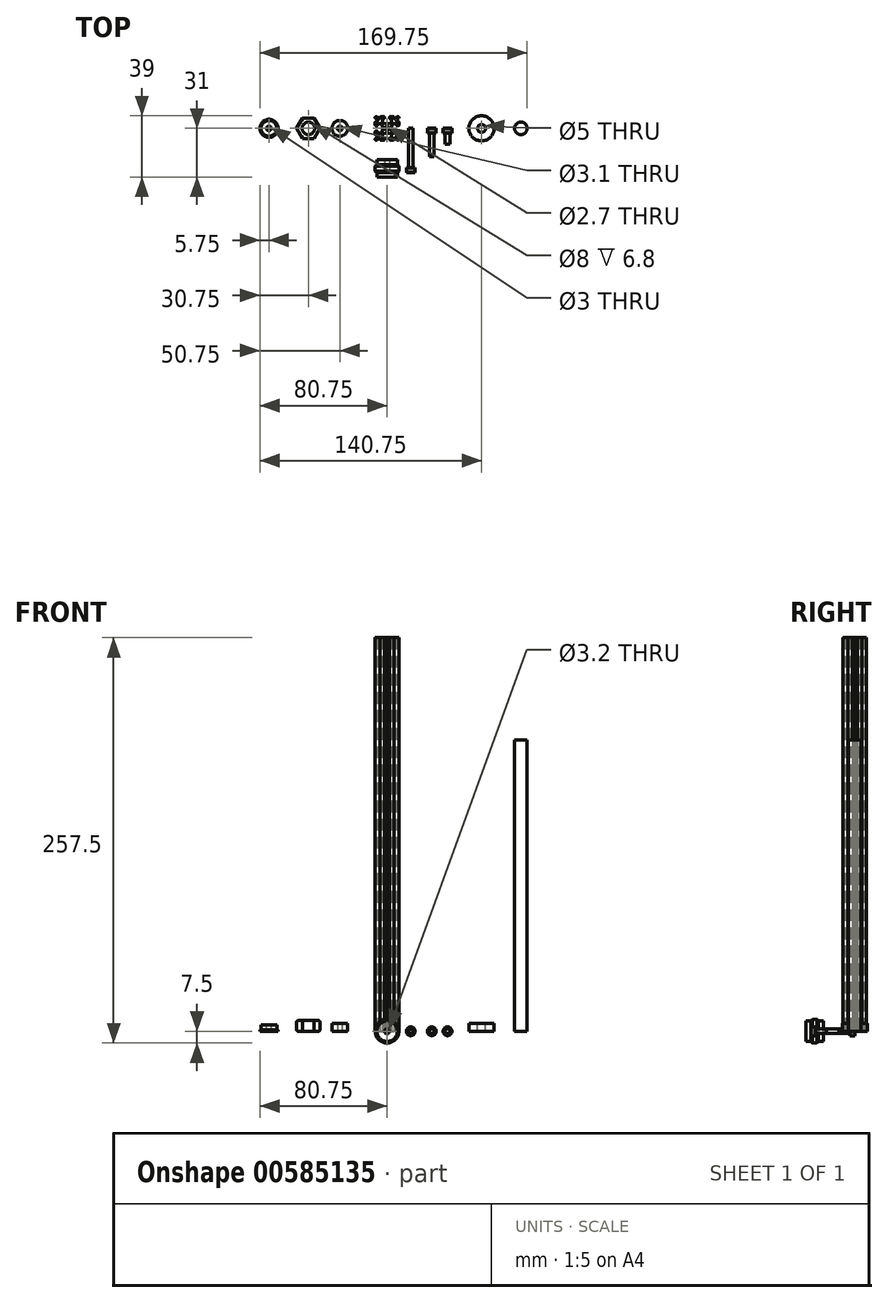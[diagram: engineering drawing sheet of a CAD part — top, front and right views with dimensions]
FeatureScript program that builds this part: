
annotation { "Feature Type Name" : "Feature", "Feature Type Description" : "" }
export const myFeature = defineFeature(function(context is Context, id is Id, definition is map)
    precondition{}
    {
        {
            var Q0;
            Q0=qCreatedBy(makeId("Top.planeOp"),FACE);
            var sketch = newSketch(context, id + "F0", { "sketchPlane" : qUnion([Q0])});
            skLineSegment(sketch, "E0", {"start": v(0, 0) * mm, "end": v(-7.5, -7.5) * mm, "construction": true});
            skArc(sketch, "E1", {"start": v(-1.35, 0) * mm, "mid": v(-1.25, -0.52) * mm, "end": v(-0.95, -0.95) * mm});
            skLineSegment(sketch, "E2", {"start": v(-7.5, -7) * mm, "end": v(-7.5, -6.72) * mm});
            skLineSegment(sketch, "E3", {"start": v(-7.35, -6.36) * mm, "end": v(-6.25, -5.26) * mm});
            skLineSegment(sketch, "E4", {"start": v(-6.6, -4.4) * mm, "end": v(-7, -4.4) * mm});
            skLineSegment(sketch, "E5", {"start": v(-7.5, -3.9) * mm, "end": v(-7.5, -2.1) * mm});
            skLineSegment(sketch, "E6", {"start": v(-7, -1.6) * mm, "end": v(-6.6, -1.6) * mm});
            skLineSegment(sketch, "E7", {"start": v(-6.1, -2.1) * mm, "end": v(-6.1, -2.7) * mm});
            skLineSegment(sketch, "E8", {"start": v(-5.9, -2.9) * mm, "end": v(-3.74, -2.9) * mm});
            skLineSegment(sketch, "E9", {"start": v(-3.25, -2.49) * mm, "end": v(-2.93, -0.73) * mm});
            skLineSegment(sketch, "E10", {"start": v(-2.73, -0.57) * mm, "end": v(-2.6, -0.57) * mm});
            skLineSegment(sketch, "E11", {"start": v(-2.4, -0.37) * mm, "end": v(-2.4, 0) * mm});
            skLineSegment(sketch, "E12", {"start": v(-2.4, 0) * mm, "end": v(-1.35, 0) * mm, "construction": true});
            skPoint(sketch, "E13.visualSharp", {"position": v(-5.4, -4.4) * mm});
            skArc(sketch, "E13.filletArc", {"start": v(-6.25, -5.26) * mm, "mid": v(-6.14, -4.71) * mm, "end": v(-6.6, -4.4) * mm});
            skPoint(sketch, "E14.visualSharp", {"position": v(-6.1, -2.9) * mm});
            skArc(sketch, "E14.filletArc", {"start": v(-6.1, -2.7) * mm, "mid": v(-6.04, -2.84) * mm, "end": v(-5.9, -2.9) * mm});
            skPoint(sketch, "E15.visualSharp", {"position": v(-6.1, -1.6) * mm});
            skArc(sketch, "E15.filletArc", {"start": v(-6.1, -2.1) * mm, "mid": v(-6.25, -1.75) * mm, "end": v(-6.6, -1.6) * mm});
            skPoint(sketch, "E16.visualSharp", {"position": v(-7.5, -1.6) * mm});
            skArc(sketch, "E16.filletArc", {"start": v(-7, -1.6) * mm, "mid": v(-7.35, -1.75) * mm, "end": v(-7.5, -2.1) * mm});
            skPoint(sketch, "E17.visualSharp", {"position": v(-7.5, -4.4) * mm});
            skArc(sketch, "E17.filletArc", {"start": v(-7.5, -3.9) * mm, "mid": v(-7.35, -4.26) * mm, "end": v(-7, -4.4) * mm});
            skPoint(sketch, "E18.visualSharp", {"position": v(-7.5, -6.51) * mm});
            skArc(sketch, "E18.filletArc", {"start": v(-7.35, -6.36) * mm, "mid": v(-7.46, -6.53) * mm, "end": v(-7.5, -6.72) * mm});
            skPoint(sketch, "E19.visualSharp", {"position": v(-3.32, -2.9) * mm});
            skArc(sketch, "E19.filletArc", {"start": v(-3.74, -2.9) * mm, "mid": v(-3.42, -2.78) * mm, "end": v(-3.25, -2.49) * mm});
            skPoint(sketch, "E20.visualSharp", {"position": v(-2.9, -0.57) * mm});
            skArc(sketch, "E20.filletArc", {"start": v(-2.73, -0.57) * mm, "mid": v(-2.86, -0.62) * mm, "end": v(-2.93, -0.73) * mm});
            skPoint(sketch, "E21.visualSharp", {"position": v(-2.4, -0.57) * mm});
            skArc(sketch, "E21.filletArc", {"start": v(-2.6, -0.57) * mm, "mid": v(-2.46, -0.51) * mm, "end": v(-2.4, -0.37) * mm});
            skLineSegment(sketch, "E22.0.MirrorCS", {"start": v(0, -2.4) * mm, "end": v(0, -1.35) * mm, "construction": true});
            skPoint(sketch, "E22.1.MirrorP", {"position": v(-4.4, -7.5) * mm});
            skArc(sketch, "E22.2.MirrorCS", {"start": v(-6.36, -7.35) * mm, "mid": v(-6.53, -7.46) * mm, "end": v(-6.72, -7.5) * mm});
            skPoint(sketch, "E22.3.MirrorP", {"position": v(-1.6, -7.5) * mm});
            skArc(sketch, "E22.4.MirrorCS", {"start": v(-1.6, -7) * mm, "mid": v(-1.75, -7.35) * mm, "end": v(-2.1, -7.5) * mm});
            skArc(sketch, "E22.5.MirrorCS", {"start": v(-0.57, -2.73) * mm, "mid": v(-0.62, -2.86) * mm, "end": v(-0.73, -2.93) * mm});
            skPoint(sketch, "E22.6.MirrorP", {"position": v(-1.6, -6.1) * mm});
            skLineSegment(sketch, "E22.7.MirrorCS", {"start": v(-3.9, -7.5) * mm, "end": v(-2.1, -7.5) * mm});
            skArc(sketch, "E22.8.MirrorCS", {"start": v(-5.26, -6.25) * mm, "mid": v(-4.71, -6.14) * mm, "end": v(-4.4, -6.6) * mm});
            skPoint(sketch, "E22.9.MirrorP", {"position": v(-0.57, -2.4) * mm});
            skPoint(sketch, "E22.10.MirrorP", {"position": v(-4.4, -5.4) * mm});
            skArc(sketch, "E22.11.MirrorCS", {"start": v(-2.7, -6.1) * mm, "mid": v(-2.84, -6.04) * mm, "end": v(-2.9, -5.9) * mm});
            skPoint(sketch, "E22.12.MirrorP", {"position": v(-0.57, -2.9) * mm});
            skLineSegment(sketch, "E22.13.MirrorCS", {"start": v(-7, -7.5) * mm, "end": v(-6.72, -7.5) * mm});
            skLineSegment(sketch, "E22.14.MirrorCS", {"start": v(-1.6, -7) * mm, "end": v(-1.6, -6.6) * mm});
            skLineSegment(sketch, "E22.15.MirrorCS", {"start": v(-6.36, -7.35) * mm, "end": v(-5.26, -6.25) * mm});
            skArc(sketch, "E22.16.MirrorCS", {"start": v(-2.1, -6.1) * mm, "mid": v(-1.75, -6.25) * mm, "end": v(-1.6, -6.6) * mm});
            skLineSegment(sketch, "E22.17.MirrorCS", {"start": v(-4.4, -6.6) * mm, "end": v(-4.4, -7) * mm});
            skArc(sketch, "E22.18.MirrorCS", {"start": v(-2.9, -3.74) * mm, "mid": v(-2.78, -3.42) * mm, "end": v(-2.49, -3.25) * mm});
            skLineSegment(sketch, "E22.19.MirrorCS", {"start": v(-2.9, -5.9) * mm, "end": v(-2.9, -3.74) * mm});
            skLineSegment(sketch, "E22.20.MirrorCS", {"start": v(-2.1, -6.1) * mm, "end": v(-2.7, -6.1) * mm});
            skArc(sketch, "E22.21.MirrorCS", {"start": v(-0.57, -2.6) * mm, "mid": v(-0.51, -2.46) * mm, "end": v(-0.37, -2.4) * mm});
            skLineSegment(sketch, "E22.22.MirrorCS", {"start": v(-0.37, -2.4) * mm, "end": v(0, -2.4) * mm});
            skPoint(sketch, "E22.23.MirrorP", {"position": v(-6.51, -7.5) * mm});
            skPoint(sketch, "E22.24.MirrorP", {"position": v(-2.9, -6.1) * mm});
            skLineSegment(sketch, "E22.25.MirrorCS", {"start": v(-2.49, -3.25) * mm, "end": v(-0.73, -2.93) * mm});
            skLineSegment(sketch, "E22.26.MirrorCS", {"start": v(-0.57, -2.73) * mm, "end": v(-0.57, -2.6) * mm});
            skArc(sketch, "E22.27.MirrorCS", {"start": v(0, -1.35) * mm, "mid": v(-0.52, -1.25) * mm, "end": v(-0.95, -0.95) * mm});
            skArc(sketch, "E22.28.MirrorCS", {"start": v(-3.9, -7.5) * mm, "mid": v(-4.26, -7.35) * mm, "end": v(-4.4, -7) * mm});
            skPoint(sketch, "E22.29.MirrorP", {"position": v(-2.9, -3.32) * mm});
            skPoint(sketch, "E23.visualSharp", {"position": v(-7.5, -7.5) * mm});
            skArc(sketch, "E23.filletArc", {"start": v(-7.5, -7) * mm, "mid": v(-7.35, -7.35) * mm, "end": v(-7, -7.5) * mm});
            skLineSegment(sketch, "E24.0.MirrorCS", {"start": v(0, 2.4) * mm, "end": v(0, 1.35) * mm, "construction": true});
            skLineSegment(sketch, "E24.1.MirrorCS", {"start": v(-2.1, 6.1) * mm, "end": v(-2.7, 6.1) * mm});
            skLineSegment(sketch, "E24.2.MirrorCS", {"start": v(-7.5, 3.9) * mm, "end": v(-7.5, 2.1) * mm});
            skLineSegment(sketch, "E24.3.MirrorCS", {"start": v(-7, 1.6) * mm, "end": v(-6.6, 1.6) * mm});
            skArc(sketch, "E24.4.MirrorCS", {"start": v(-6.1, 2.1) * mm, "mid": v(-6.25, 1.75) * mm, "end": v(-6.6, 1.6) * mm});
            skPoint(sketch, "E24.5.MirrorP", {"position": v(-3.32, 2.9) * mm});
            skPoint(sketch, "E24.6.MirrorP", {"position": v(-0.57, 2.9) * mm});
            skArc(sketch, "E24.7.MirrorCS", {"start": v(-0.57, 2.6) * mm, "mid": v(-0.51, 2.46) * mm, "end": v(-0.37, 2.4) * mm});
            skArc(sketch, "E24.8.MirrorCS", {"start": v(-2.6, 0.57) * mm, "mid": v(-2.46, 0.51) * mm, "end": v(-2.4, 0.37) * mm});
            skLineSegment(sketch, "E24.9.MirrorCS", {"start": v(-0.37, 2.4) * mm, "end": v(0, 2.4) * mm});
            skArc(sketch, "E24.10.MirrorCS", {"start": v(-6.1, 2.7) * mm, "mid": v(-6.04, 2.84) * mm, "end": v(-5.9, 2.9) * mm});
            skPoint(sketch, "E24.11.MirrorP", {"position": v(-4.4, 5.4) * mm});
            skLineSegment(sketch, "E24.12.MirrorCS", {"start": v(-2.9, 5.9) * mm, "end": v(-2.9, 3.74) * mm});
            skLineSegment(sketch, "E24.13.MirrorCS", {"start": v(-7.35, 6.36) * mm, "end": v(-6.25, 5.26) * mm});
            skPoint(sketch, "E24.14.MirrorP", {"position": v(-7.5, 6.51) * mm});
            skArc(sketch, "E24.15.MirrorCS", {"start": v(-3.74, 2.9) * mm, "mid": v(-3.42, 2.78) * mm, "end": v(-3.25, 2.49) * mm});
            skArc(sketch, "E24.16.MirrorCS", {"start": v(-2.1, 6.1) * mm, "mid": v(-1.75, 6.25) * mm, "end": v(-1.6, 6.6) * mm});
            skArc(sketch, "E24.17.MirrorCS", {"start": v(-7, 1.6) * mm, "mid": v(-7.35, 1.75) * mm, "end": v(-7.5, 2.1) * mm});
            skPoint(sketch, "E24.18.MirrorP", {"position": v(-1.6, 6.1) * mm});
            skPoint(sketch, "E24.19.MirrorP", {"position": v(-7.5, 4.4) * mm});
            skLineSegment(sketch, "E24.20.MirrorCS", {"start": v(-4.4, 6.6) * mm, "end": v(-4.4, 7) * mm});
            skArc(sketch, "E24.21.MirrorCS", {"start": v(-7.5, 3.9) * mm, "mid": v(-7.35, 4.26) * mm, "end": v(-7, 4.4) * mm});
            skPoint(sketch, "E24.22.MirrorP", {"position": v(-0.57, 2.4) * mm});
            skLineSegment(sketch, "E24.23.MirrorCS", {"start": v(-5.9, 2.9) * mm, "end": v(-3.74, 2.9) * mm});
            skArc(sketch, "E24.24.MirrorCS", {"start": v(-2.9, 3.74) * mm, "mid": v(-2.78, 3.42) * mm, "end": v(-2.49, 3.25) * mm});
            skArc(sketch, "E24.25.MirrorCS", {"start": v(-7.35, 6.36) * mm, "mid": v(-7.46, 6.53) * mm, "end": v(-7.5, 6.72) * mm});
            skPoint(sketch, "E24.26.MirrorP", {"position": v(-6.1, 2.9) * mm});
            skPoint(sketch, "E24.27.MirrorP", {"position": v(-4.4, 7.5) * mm});
            skArc(sketch, "E24.28.MirrorCS", {"start": v(-5.26, 6.25) * mm, "mid": v(-4.71, 6.14) * mm, "end": v(-4.4, 6.6) * mm});
            skArc(sketch, "E24.29.MirrorCS", {"start": v(-7.5, 7) * mm, "mid": v(-7.35, 7.35) * mm, "end": v(-7, 7.5) * mm});
            skPoint(sketch, "E24.30.MirrorP", {"position": v(-6.1, 1.6) * mm});
            skPoint(sketch, "E24.31.MirrorP", {"position": v(-2.9, 3.32) * mm});
            skPoint(sketch, "E24.32.MirrorP", {"position": v(-1.6, 7.5) * mm});
            skPoint(sketch, "E24.33.MirrorP", {"position": v(-2.9, 6.1) * mm});
            skLineSegment(sketch, "E24.34.MirrorCS", {"start": v(-3.9, 7.5) * mm, "end": v(-2.1, 7.5) * mm});
            skLineSegment(sketch, "E24.35.MirrorCS", {"start": v(-7, 7.5) * mm, "end": v(-6.72, 7.5) * mm});
            skArc(sketch, "E24.36.MirrorCS", {"start": v(-3.9, 7.5) * mm, "mid": v(-4.26, 7.35) * mm, "end": v(-4.4, 7) * mm});
            skPoint(sketch, "E24.37.MirrorP", {"position": v(-7.5, 7.5) * mm});
            skLineSegment(sketch, "E24.38.MirrorCS", {"start": v(-1.6, 7) * mm, "end": v(-1.6, 6.6) * mm});
            skLineSegment(sketch, "E24.39.MirrorCS", {"start": v(-6.36, 7.35) * mm, "end": v(-5.26, 6.25) * mm});
            skPoint(sketch, "E24.40.MirrorP", {"position": v(-7.5, 1.6) * mm});
            skArc(sketch, "E24.41.MirrorCS", {"start": v(-2.7, 6.1) * mm, "mid": v(-2.84, 6.04) * mm, "end": v(-2.9, 5.9) * mm});
            skArc(sketch, "E24.42.MirrorCS", {"start": v(-6.36, 7.35) * mm, "mid": v(-6.53, 7.46) * mm, "end": v(-6.72, 7.5) * mm});
            skLineSegment(sketch, "E24.43.MirrorCS", {"start": v(-2.49, 3.25) * mm, "end": v(-0.73, 2.93) * mm});
            skPoint(sketch, "E24.44.MirrorP", {"position": v(-2.9, 0.57) * mm});
            skLineSegment(sketch, "E24.45.MirrorCS", {"start": v(-6.6, 4.4) * mm, "end": v(-7, 4.4) * mm});
            skArc(sketch, "E24.46.MirrorCS", {"start": v(-1.6, 7) * mm, "mid": v(-1.75, 7.35) * mm, "end": v(-2.1, 7.5) * mm});
            skArc(sketch, "E24.47.MirrorCS", {"start": v(-2.73, 0.57) * mm, "mid": v(-2.86, 0.62) * mm, "end": v(-2.93, 0.73) * mm});
            skArc(sketch, "E24.48.MirrorCS", {"start": v(-6.25, 5.26) * mm, "mid": v(-6.14, 4.71) * mm, "end": v(-6.6, 4.4) * mm});
            skLineSegment(sketch, "E24.49.MirrorCS", {"start": v(-0.57, 2.73) * mm, "end": v(-0.57, 2.6) * mm});
            skLineSegment(sketch, "E24.50.MirrorCS", {"start": v(-2.73, 0.57) * mm, "end": v(-2.6, 0.57) * mm});
            skArc(sketch, "E24.51.MirrorCS", {"start": v(-1.35, 0) * mm, "mid": v(-1.25, 0.52) * mm, "end": v(-0.95, 0.95) * mm});
            skPoint(sketch, "E24.52.MirrorP", {"position": v(-2.4, 0.57) * mm});
            skPoint(sketch, "E24.53.MirrorP", {"position": v(-5.4, 4.4) * mm});
            skLineSegment(sketch, "E24.54.MirrorCS", {"start": v(-2.4, 0.37) * mm, "end": v(-2.4, 0) * mm});
            skArc(sketch, "E24.55.MirrorCS", {"start": v(0, 1.35) * mm, "mid": v(-0.52, 1.25) * mm, "end": v(-0.95, 0.95) * mm});
            skLineSegment(sketch, "E24.56.MirrorCS", {"start": v(-3.25, 2.49) * mm, "end": v(-2.93, 0.73) * mm});
            skLineSegment(sketch, "E24.57.MirrorCS", {"start": v(-6.1, 2.1) * mm, "end": v(-6.1, 2.7) * mm});
            skLineSegment(sketch, "E24.58.MirrorCS", {"start": v(-7.5, 7) * mm, "end": v(-7.5, 6.72) * mm});
            skArc(sketch, "E24.59.MirrorCS", {"start": v(-0.57, 2.73) * mm, "mid": v(-0.62, 2.86) * mm, "end": v(-0.73, 2.93) * mm});
            skPoint(sketch, "E24.60.MirrorP", {"position": v(-6.51, 7.5) * mm});
            skLineSegment(sketch, "E25.0.MirrorCS", {"start": v(7, -7.5) * mm, "end": v(6.72, -7.5) * mm});
            skLineSegment(sketch, "E25.1.MirrorCS", {"start": v(0.57, 2.73) * mm, "end": v(0.57, 2.6) * mm});
            skLineSegment(sketch, "E25.2.MirrorCS", {"start": v(0.37, 2.4) * mm, "end": v(0, 2.4) * mm});
            skLineSegment(sketch, "E25.3.MirrorCS", {"start": v(7, 7.5) * mm, "end": v(6.72, 7.5) * mm});
            skLineSegment(sketch, "E25.4.MirrorCS", {"start": v(1.6, -7) * mm, "end": v(1.6, -6.6) * mm});
            skLineSegment(sketch, "E25.5.MirrorCS", {"start": v(2.73, 0.57) * mm, "end": v(2.6, 0.57) * mm});
            skLineSegment(sketch, "E25.6.MirrorCS", {"start": v(7, 1.6) * mm, "end": v(6.6, 1.6) * mm});
            skLineSegment(sketch, "E25.7.MirrorCS", {"start": v(5.9, 2.9) * mm, "end": v(3.74, 2.9) * mm});
            skLineSegment(sketch, "E25.8.MirrorCS", {"start": v(7.35, 6.36) * mm, "end": v(6.25, 5.26) * mm});
            skArc(sketch, "E25.9.MirrorCS", {"start": v(2.7, -6.1) * mm, "mid": v(2.84, -6.04) * mm, "end": v(2.9, -5.9) * mm});
            skArc(sketch, "E25.10.MirrorCS", {"start": v(2.9, 3.74) * mm, "mid": v(2.78, 3.42) * mm, "end": v(2.49, 3.25) * mm});
            skPoint(sketch, "E25.11.MirrorP", {"position": v(1.6, -7.5) * mm});
            skPoint(sketch, "E25.12.MirrorP", {"position": v(6.1, -1.6) * mm});
            skPoint(sketch, "E25.13.MirrorP", {"position": v(2.9, 3.32) * mm});
            skPoint(sketch, "E25.14.MirrorP", {"position": v(7.5, -1.6) * mm});
            skArc(sketch, "E25.15.MirrorCS", {"start": v(1.6, 7) * mm, "mid": v(1.75, 7.35) * mm, "end": v(2.1, 7.5) * mm});
            skLineSegment(sketch, "E25.16.MirrorCS", {"start": v(6.1, -2.1) * mm, "end": v(6.1, -2.7) * mm});
            skLineSegment(sketch, "E25.17.MirrorCS", {"start": v(2.4, 0.37) * mm, "end": v(2.4, 0) * mm});
            skArc(sketch, "E25.18.MirrorCS", {"start": v(7, -1.6) * mm, "mid": v(7.35, -1.75) * mm, "end": v(7.5, -2.1) * mm});
            skArc(sketch, "E25.19.MirrorCS", {"start": v(7.5, 7) * mm, "mid": v(7.35, 7.35) * mm, "end": v(7, 7.5) * mm});
            skArc(sketch, "E25.20.MirrorCS", {"start": v(2.1, -6.1) * mm, "mid": v(1.75, -6.25) * mm, "end": v(1.6, -6.6) * mm});
            skArc(sketch, "E25.21.MirrorCS", {"start": v(6.1, 2.1) * mm, "mid": v(6.25, 1.75) * mm, "end": v(6.6, 1.6) * mm});
            skLineSegment(sketch, "E25.22.MirrorCS", {"start": v(4.4, 6.6) * mm, "end": v(4.4, 7) * mm});
            skLineSegment(sketch, "E25.23.MirrorCS", {"start": v(6.6, 4.4) * mm, "end": v(7, 4.4) * mm});
            skArc(sketch, "E25.24.MirrorCS", {"start": v(7, 1.6) * mm, "mid": v(7.35, 1.75) * mm, "end": v(7.5, 2.1) * mm});
            skArc(sketch, "E25.25.MirrorCS", {"start": v(0, -1.35) * mm, "mid": v(0.52, -1.25) * mm, "end": v(0.95, -0.95) * mm});
            skLineSegment(sketch, "E25.26.MirrorCS", {"start": v(3.9, -7.5) * mm, "end": v(2.1, -7.5) * mm});
            skLineSegment(sketch, "E25.27.MirrorCS", {"start": v(2.1, 6.1) * mm, "end": v(2.7, 6.1) * mm});
            skLineSegment(sketch, "E25.28.MirrorCS", {"start": v(2.73, -0.57) * mm, "end": v(2.6, -0.57) * mm});
            skLineSegment(sketch, "E25.29.MirrorCS", {"start": v(4.4, -6.6) * mm, "end": v(4.4, -7) * mm});
            skLineSegment(sketch, "E25.30.MirrorCS", {"start": v(3.9, 7.5) * mm, "end": v(2.1, 7.5) * mm});
            skArc(sketch, "E25.31.MirrorCS", {"start": v(0.57, -2.73) * mm, "mid": v(0.62, -2.86) * mm, "end": v(0.73, -2.93) * mm});
            skArc(sketch, "E25.32.MirrorCS", {"start": v(0.57, 2.6) * mm, "mid": v(0.51, 2.46) * mm, "end": v(0.37, 2.4) * mm});
            skPoint(sketch, "E25.33.MirrorP", {"position": v(6.51, -7.5) * mm});
            skArc(sketch, "E25.34.MirrorCS", {"start": v(3.9, -7.5) * mm, "mid": v(4.26, -7.35) * mm, "end": v(4.4, -7) * mm});
            skArc(sketch, "E25.35.MirrorCS", {"start": v(2.7, 6.1) * mm, "mid": v(2.84, 6.04) * mm, "end": v(2.9, 5.9) * mm});
            skPoint(sketch, "E25.36.MirrorP", {"position": v(0.57, -2.4) * mm});
            skPoint(sketch, "E25.37.MirrorP", {"position": v(0.57, 2.9) * mm});
            skLineSegment(sketch, "E25.38.MirrorCS", {"start": v(3.25, -2.49) * mm, "end": v(2.93, -0.73) * mm});
            skPoint(sketch, "E25.39.MirrorP", {"position": v(5.4, -4.4) * mm});
            skPoint(sketch, "E25.40.MirrorP", {"position": v(2.4, -0.57) * mm});
            skLineSegment(sketch, "E25.41.MirrorCS", {"start": v(7.5, -7) * mm, "end": v(7.5, -6.72) * mm});
            skArc(sketch, "E25.42.MirrorCS", {"start": v(7.35, 6.36) * mm, "mid": v(7.46, 6.53) * mm, "end": v(7.5, 6.72) * mm});
            skPoint(sketch, "E25.43.MirrorP", {"position": v(4.4, 7.5) * mm});
            skArc(sketch, "E25.44.MirrorCS", {"start": v(6.25, 5.26) * mm, "mid": v(6.14, 4.71) * mm, "end": v(6.6, 4.4) * mm});
            skPoint(sketch, "E25.45.MirrorP", {"position": v(6.1, -2.9) * mm});
            skPoint(sketch, "E25.46.MirrorP", {"position": v(4.4, -7.5) * mm});
            skArc(sketch, "E25.47.MirrorCS", {"start": v(6.1, 2.7) * mm, "mid": v(6.04, 2.84) * mm, "end": v(5.9, 2.9) * mm});
            skLineSegment(sketch, "E25.48.MirrorCS", {"start": v(2.1, -6.1) * mm, "end": v(2.7, -6.1) * mm});
            skArc(sketch, "E25.49.MirrorCS", {"start": v(2.73, -0.57) * mm, "mid": v(2.86, -0.62) * mm, "end": v(2.93, -0.73) * mm});
            skArc(sketch, "E25.50.MirrorCS", {"start": v(7.35, -6.36) * mm, "mid": v(7.46, -6.53) * mm, "end": v(7.5, -6.72) * mm});
            skLineSegment(sketch, "E25.51.MirrorCS", {"start": v(3.25, 2.49) * mm, "end": v(2.93, 0.73) * mm});
            skArc(sketch, "E25.52.MirrorCS", {"start": v(2.9, -3.74) * mm, "mid": v(2.78, -3.42) * mm, "end": v(2.49, -3.25) * mm});
            skArc(sketch, "E25.53.MirrorCS", {"start": v(2.6, 0.57) * mm, "mid": v(2.46, 0.51) * mm, "end": v(2.4, 0.37) * mm});
            skPoint(sketch, "E25.54.MirrorP", {"position": v(2.9, 0.57) * mm});
            skPoint(sketch, "E25.55.MirrorP", {"position": v(7.5, -6.51) * mm});
            skLineSegment(sketch, "E25.56.MirrorCS", {"start": v(2.49, 3.25) * mm, "end": v(0.73, 2.93) * mm});
            skArc(sketch, "E25.57.MirrorCS", {"start": v(1.6, -7) * mm, "mid": v(1.75, -7.35) * mm, "end": v(2.1, -7.5) * mm});
            skArc(sketch, "E25.58.MirrorCS", {"start": v(2.1, 6.1) * mm, "mid": v(1.75, 6.25) * mm, "end": v(1.6, 6.6) * mm});
            skLineSegment(sketch, "E25.59.MirrorCS", {"start": v(0.57, -2.73) * mm, "end": v(0.57, -2.6) * mm});
            skLineSegment(sketch, "E25.60.MirrorCS", {"start": v(2.4, -0.37) * mm, "end": v(2.4, 0) * mm});
            skArc(sketch, "E25.61.MirrorCS", {"start": v(7.5, -3.9) * mm, "mid": v(7.35, -4.26) * mm, "end": v(7, -4.4) * mm});
            skLineSegment(sketch, "E25.62.MirrorCS", {"start": v(5.9, -2.9) * mm, "end": v(3.74, -2.9) * mm});
            skLineSegment(sketch, "E25.63.MirrorCS", {"start": v(7.5, -3.9) * mm, "end": v(7.5, -2.1) * mm});
            skLineSegment(sketch, "E25.64.MirrorCS", {"start": v(7, -1.6) * mm, "end": v(6.6, -1.6) * mm});
            skArc(sketch, "E25.65.MirrorCS", {"start": v(1.35, 0) * mm, "mid": v(1.25, -0.52) * mm, "end": v(0.95, -0.95) * mm});
            skPoint(sketch, "E25.66.MirrorP", {"position": v(7.5, 1.6) * mm});
            skPoint(sketch, "E25.67.MirrorP", {"position": v(1.6, 6.1) * mm});
            skLineSegment(sketch, "E25.68.MirrorCS", {"start": v(6.36, -7.35) * mm, "end": v(5.26, -6.25) * mm});
            skPoint(sketch, "E25.69.MirrorP", {"position": v(2.4, 0.57) * mm});
            skPoint(sketch, "E25.70.MirrorP", {"position": v(6.1, 1.6) * mm});
            skPoint(sketch, "E25.71.MirrorP", {"position": v(3.32, -2.9) * mm});
            skPoint(sketch, "E25.72.MirrorP", {"position": v(0.57, -2.9) * mm});
            skPoint(sketch, "E25.73.MirrorP", {"position": v(7.5, 4.4) * mm});
            skArc(sketch, "E25.74.MirrorCS", {"start": v(5.26, -6.25) * mm, "mid": v(4.71, -6.14) * mm, "end": v(4.4, -6.6) * mm});
            skArc(sketch, "E25.75.MirrorCS", {"start": v(7.5, -7) * mm, "mid": v(7.35, -7.35) * mm, "end": v(7, -7.5) * mm});
            skLineSegment(sketch, "E25.76.MirrorCS", {"start": v(2.49, -3.25) * mm, "end": v(0.73, -2.93) * mm});
            skArc(sketch, "E25.77.MirrorCS", {"start": v(3.74, 2.9) * mm, "mid": v(3.42, 2.78) * mm, "end": v(3.25, 2.49) * mm});
            skArc(sketch, "E25.78.MirrorCS", {"start": v(6.36, -7.35) * mm, "mid": v(6.53, -7.46) * mm, "end": v(6.72, -7.5) * mm});
            skArc(sketch, "E25.79.MirrorCS", {"start": v(7.5, 3.9) * mm, "mid": v(7.35, 4.26) * mm, "end": v(7, 4.4) * mm});
            skArc(sketch, "E25.80.MirrorCS", {"start": v(2.73, 0.57) * mm, "mid": v(2.86, 0.62) * mm, "end": v(2.93, 0.73) * mm});
            skArc(sketch, "E25.81.MirrorCS", {"start": v(6.36, 7.35) * mm, "mid": v(6.53, 7.46) * mm, "end": v(6.72, 7.5) * mm});
            skPoint(sketch, "E25.82.MirrorP", {"position": v(4.4, -5.4) * mm});
            skPoint(sketch, "E25.83.MirrorP", {"position": v(6.51, 7.5) * mm});
            skPoint(sketch, "E25.84.MirrorP", {"position": v(2.9, -0.57) * mm});
            skLineSegment(sketch, "E25.85.MirrorCS", {"start": v(2.9, -5.9) * mm, "end": v(2.9, -3.74) * mm});
            skLineSegment(sketch, "E25.86.MirrorCS", {"start": v(6.1, 2.1) * mm, "end": v(6.1, 2.7) * mm});
            skLineSegment(sketch, "E25.87.MirrorCS", {"start": v(6.36, 7.35) * mm, "end": v(5.26, 6.25) * mm});
            skArc(sketch, "E25.88.MirrorCS", {"start": v(0.57, 2.73) * mm, "mid": v(0.62, 2.86) * mm, "end": v(0.73, 2.93) * mm});
            skArc(sketch, "E25.89.MirrorCS", {"start": v(0.57, -2.6) * mm, "mid": v(0.51, -2.46) * mm, "end": v(0.37, -2.4) * mm});
            skLineSegment(sketch, "E25.90.MirrorCS", {"start": v(2.9, 5.9) * mm, "end": v(2.9, 3.74) * mm});
            skArc(sketch, "E25.91.MirrorCS", {"start": v(0, 1.35) * mm, "mid": v(0.52, 1.25) * mm, "end": v(0.95, 0.95) * mm});
            skArc(sketch, "E25.92.MirrorCS", {"start": v(2.6, -0.57) * mm, "mid": v(2.46, -0.51) * mm, "end": v(2.4, -0.37) * mm});
            skPoint(sketch, "E25.93.MirrorP", {"position": v(4.4, 5.4) * mm});
            skPoint(sketch, "E25.94.MirrorP", {"position": v(2.9, -3.32) * mm});
            skPoint(sketch, "E25.95.MirrorP", {"position": v(2.9, 6.1) * mm});
            skPoint(sketch, "E25.96.MirrorP", {"position": v(5.4, 4.4) * mm});
            skPoint(sketch, "E25.97.MirrorP", {"position": v(3.32, 2.9) * mm});
            skArc(sketch, "E25.98.MirrorCS", {"start": v(3.74, -2.9) * mm, "mid": v(3.42, -2.78) * mm, "end": v(3.25, -2.49) * mm});
            skArc(sketch, "E25.99.MirrorCS", {"start": v(3.9, 7.5) * mm, "mid": v(4.26, 7.35) * mm, "end": v(4.4, 7) * mm});
            skPoint(sketch, "E25.100.MirrorP", {"position": v(7.5, -4.4) * mm});
            skPoint(sketch, "E25.101.MirrorP", {"position": v(6.1, 2.9) * mm});
            skArc(sketch, "E25.102.MirrorCS", {"start": v(1.35, 0) * mm, "mid": v(1.25, 0.52) * mm, "end": v(0.95, 0.95) * mm});
            skArc(sketch, "E25.103.MirrorCS", {"start": v(5.26, 6.25) * mm, "mid": v(4.71, 6.14) * mm, "end": v(4.4, 6.6) * mm});
            skPoint(sketch, "E25.104.MirrorP", {"position": v(7.5, 6.51) * mm});
            skPoint(sketch, "E25.105.MirrorP", {"position": v(2.9, -6.1) * mm});
            skArc(sketch, "E25.106.MirrorCS", {"start": v(6.25, -5.26) * mm, "mid": v(6.14, -4.71) * mm, "end": v(6.6, -4.4) * mm});
            skArc(sketch, "E25.107.MirrorCS", {"start": v(6.1, -2.1) * mm, "mid": v(6.25, -1.75) * mm, "end": v(6.6, -1.6) * mm});
            skPoint(sketch, "E25.108.MirrorP", {"position": v(1.6, 7.5) * mm});
            skPoint(sketch, "E25.109.MirrorP", {"position": v(7.5, 7.5) * mm});
            skLineSegment(sketch, "E25.110.MirrorCS", {"start": v(0.37, -2.4) * mm, "end": v(0, -2.4) * mm});
            skPoint(sketch, "E25.111.MirrorP", {"position": v(7.5, -7.5) * mm});
            skLineSegment(sketch, "E25.112.MirrorCS", {"start": v(7.5, 7) * mm, "end": v(7.5, 6.72) * mm});
            skArc(sketch, "E25.113.MirrorCS", {"start": v(6.1, -2.7) * mm, "mid": v(6.04, -2.84) * mm, "end": v(5.9, -2.9) * mm});
            skLineSegment(sketch, "E25.114.MirrorCS", {"start": v(1.6, 7) * mm, "end": v(1.6, 6.6) * mm});
            skPoint(sketch, "E25.115.MirrorP", {"position": v(1.6, -6.1) * mm});
            skLineSegment(sketch, "E25.116.MirrorCS", {"start": v(7.35, -6.36) * mm, "end": v(6.25, -5.26) * mm});
            skLineSegment(sketch, "E25.117.MirrorCS", {"start": v(7.5, 3.9) * mm, "end": v(7.5, 2.1) * mm});
            skPoint(sketch, "E25.118.MirrorP", {"position": v(0.57, 2.4) * mm});
            skLineSegment(sketch, "E25.119.MirrorCS", {"start": v(6.6, -4.4) * mm, "end": v(7, -4.4) * mm});
            skSolve(sketch);
        }
        {
            var Q0;
            Q0=makeQuery(id+"F0.imprint","IMPRINT",FACE,{"disambiguationData":[TD([[makeQuery(id+"F0.imprint","IMPRINT",EDGE,{"derivedFrom":sQuery(id+"F0.wireOp",EDGE,"E1")}),-1.0]])]});
            extrude(context, id + "F1", {"entities" : qUnion([Q0]), "depth" : 250 * mm});
        }
        {
            var Q0;
            Q0=qCreatedBy(makeId("Right.planeOp"),FACE);
            var sketch = newSketch(context, id + "F2", { "sketchPlane" : qUnion([Q0])});
            skLineSegment(sketch, "E26", {"start": v(-31, 0) * mm, "end": v(-31, 6.5) * mm});
            skLineSegment(sketch, "E27", {"start": v(-20, 6.5) * mm, "end": v(-20, 0) * mm});
            skLineSegment(sketch, "E28", {"start": v(-20, 0) * mm, "end": v(-31, 0) * mm});
            skLineSegment(sketch, "E29", {"start": v(-31, 6.5) * mm, "end": v(-28, 6.5) * mm});
            skLineSegment(sketch, "E30", {"start": v(-28, 6.5) * mm, "end": v(-27, 7.5) * mm});
            skLineSegment(sketch, "E31", {"start": v(-27, 7.5) * mm, "end": v(-24, 7.5) * mm});
            skLineSegment(sketch, "E32", {"start": v(-24, 7.5) * mm, "end": v(-23, 6.5) * mm});
            skLineSegment(sketch, "E33", {"start": v(-23, 6.5) * mm, "end": v(-20, 6.5) * mm});
            skLineSegment(sketch, "E34", {"start": v(-25.5, 7.5) * mm, "end": v(-25.5, 0) * mm, "construction": true});
            skSolve(sketch);
        }
        {
            var Q0;
            Q0=qSketchRegion(id+"F2",true);
            var Q1;
            Q1=sQuery(id+"F2.wireOp",EDGE,"E28");
            revolve(context, id + "F3", {"entities" : qUnion([Q0]), "axis" : qUnion([Q1]), "revolveType" : RevolveType.FULL});
        }
        {
            var Q0;
            Q0=makeQuery(id+"F3.opRevolve","SWEPT_FACE",FACE,{"disambiguationData":[OSD([sQuery(id+"F2.wireOp",EDGE,"E26")])]});
            var sketch = newSketch(context, id + "F4", { "sketchPlane" : qUnion([Q0])});
            skCircle(sketch, "E35", {"center": v(0, 0) * mm, "radius": 1.6 * mm});
            skSolve(sketch);
        }
        {
            var Q0;
            Q0=makeQuery(id+"F4.imprint","IMPRINT",FACE,{"disambiguationData":[TD([[makeQuery(id+"F4.imprint","IMPRINT",EDGE,{"derivedFrom":sQuery(id+"F4.wireOp",EDGE,"E35")}),1.0]])]});
            extrude(context, id + "F5", {"entities" : qUnion([Q0]), "operationType" : NewBodyOperationType.REMOVE, "oppositeDirection" : true, "depth" : 11 * mm});
        }
        {
            var Q0;
            Q0=qCreatedBy(makeId("Front.planeOp"),FACE);
            var sketch = newSketch(context, id + "F6", { "sketchPlane" : qUnion([Q0])});
            skCircle(sketch, "E36", {"center": v(15, 0) * mm, "radius": 1.5 * mm});
            skSolve(sketch);
        }
        {
            var Q0;
            Q0=makeQuery(id+"F6.imprint","IMPRINT",FACE,{"disambiguationData":[TD([[makeQuery(id+"F6.imprint","IMPRINT",EDGE,{"derivedFrom":sQuery(id+"F6.wireOp",EDGE,"E36")}),1.0]])]});
            extrude(context, id + "F7", {"entities" : qUnion([Q0]), "depth" : 25 * mm});
        }
        {
            var Q0;
            Q0=makeQuery(id+"F7.opExtrude","CAP_FACE",FACE,{"disambiguationData":[OSD([sQuery(id+"F6.wireOp",EDGE,"E36")])],"isStart":false});
            var sketch = newSketch(context, id + "F8", { "sketchPlane" : qUnion([Q0])});
            skCircle(sketch, "E37", {"center": v(15, 0) * mm, "radius": 2.8 * mm});
            skSolve(sketch);
        }
        {
            var Q0;
            Q0=makeQuery(id+"F8.imprint","IMPRINT",FACE,{"disambiguationData":[TD([[makeQuery(id+"F8.imprint","IMPRINT",EDGE,{"derivedFrom":sQuery(id+"F8.wireOp",EDGE,"E37")}),1.0]])]});
            var Q1;
            Q1=makeQuery(id+"F8.imprint","IMPRINT",FACE,{"disambiguationData":[TD([[makeQuery(id+"F8.imprint","IMPRINT",EDGE,{"derivedFrom":makeQuery(id+"F7.opExtrude","CAP_EDGE",EDGE,{"disambiguationData":[OSD([sQuery(id+"F6.wireOp",EDGE,"E36")])],"isStart":false})}),1.0]])]});
            extrude(context, id + "F9", {"entities" : qUnion([Q0, Q1]), "operationType" : NewBodyOperationType.ADD, "depth" : 3 * mm});
        }
        {
            var Q0;
            Q0=qCreatedBy(makeId("Top.planeOp"),FACE);
            var sketch = newSketch(context, id + "F10", { "sketchPlane" : qUnion([Q0])});
            skCircle(sketch, "E38", {"center": v(-30, 0) * mm, "radius": 5 * mm});
            skCircle(sketch, "E39", {"center": v(-30, 0) * mm, "radius": 1.55 * mm});
            skSolve(sketch);
        }
        {
            var Q0;
            Q0=makeQuery(id+"F10.imprint","IMPRINT",FACE,{"disambiguationData":[TD([[makeQuery(id+"F10.imprint","IMPRINT",EDGE,{"derivedFrom":sQuery(id+"F10.wireOp",EDGE,"E38")}),1.0]])]});
            extrude(context, id + "F11", {"entities" : qUnion([Q0]), "depth" : 5 * mm});
        }
        {
            var Q0;
            Q0=makeQuery(id+"F7.opExtrude","SWEPT_BODY",BODY,{"disambiguationData":[OSD([sQuery(id+"F6.wireOp",EDGE,"E36")])]});
            transform(context, id + "F12", {"entities" : qUnion([Q0]), "transformType" : TransformType.TRANSLATION_3D, "dx" : 13.4 * mm, "dy" : 0 * mm, "dz" : 0 * mm, "makeCopy" : true});
        }
        {
            var Q0;
            Q0=makeQuery(id+"F12.opPattern","COPY",BODY,{"derivedFrom":makeQuery(id+"F7.opExtrude","SWEPT_BODY",BODY,{"disambiguationData":[OSD([sQuery(id+"F6.wireOp",EDGE,"E36")])]}),"instanceName":"1"});
            deleteBodies(context, id + "F13", {"entities" : qUnion([Q0])});
        }
        {
            var Q0;
            Q0=qCreatedBy(makeId("Front.planeOp"),FACE);
            var sketch = newSketch(context, id + "F14", { "sketchPlane" : qUnion([Q0])});
            skCircle(sketch, "E40", {"center": v(28.37, 0) * mm, "radius": 2.8 * mm});
            skSolve(sketch);
        }
        {
            var Q0;
            Q0=makeQuery(id+"F14.imprint","IMPRINT",FACE,{"disambiguationData":[TD([[makeQuery(id+"F14.imprint","IMPRINT",EDGE,{"derivedFrom":sQuery(id+"F14.wireOp",EDGE,"E40")}),1.0]])]});
            extrude(context, id + "F15", {"entities" : qUnion([Q0]), "depth" : 3 * mm});
        }
        {
            var Q0;
            Q0=makeQuery(id+"F15.opExtrude","CAP_FACE",FACE,{"disambiguationData":[OSD([sQuery(id+"F14.wireOp",EDGE,"E40")])],"isStart":false});
            var sketch = newSketch(context, id + "F16", { "sketchPlane" : qUnion([Q0])});
            skCircle(sketch, "E41", {"center": v(28.37, 0) * mm, "radius": 1.5 * mm});
            skSolve(sketch);
        }
        {
            var Q0;
            Q0=makeQuery(id+"F16.imprint","IMPRINT",FACE,{"disambiguationData":[TD([[makeQuery(id+"F16.imprint","IMPRINT",EDGE,{"derivedFrom":sQuery(id+"F16.wireOp",EDGE,"E41")}),1.0]])]});
            extrude(context, id + "F17", {"entities" : qUnion([Q0]), "operationType" : NewBodyOperationType.ADD, "depth" : 15 * mm});
        }
        {
            var Q0;
            Q0=makeQuery(id+"F9.opExtrude","CAP_FACE",FACE,{"disambiguationData":[OSD([sQuery(id+"F8.wireOp",EDGE,"E37")])],"isStart":false});
            var sketch = newSketch(context, id + "F18", { "sketchPlane" : qUnion([Q0])});
            skCircle(sketch, "E42.cCircle", {"center": v(15, 0) * mm, "radius": 1.53 * mm, "construction": true});
            skLineSegment(sketch, "E42.0", {"start": v(15.88, -1.53) * mm, "end": v(14.12, -1.53) * mm});
            skLineSegment(sketch, "E42.1", {"start": v(14.12, -1.53) * mm, "end": v(13.24, 0) * mm});
            skLineSegment(sketch, "E42.2", {"start": v(13.24, 0) * mm, "end": v(14.12, 1.53) * mm});
            skLineSegment(sketch, "E42.3", {"start": v(14.12, 1.53) * mm, "end": v(15.88, 1.53) * mm});
            skLineSegment(sketch, "E42.4", {"start": v(15.88, 1.53) * mm, "end": v(16.76, 0) * mm});
            skLineSegment(sketch, "E42.5", {"start": v(16.76, 0) * mm, "end": v(15.88, -1.53) * mm});
            skPoint(sketch, "E42.0.midPoint", {"position": v(15, -1.53) * mm});
            skSolve(sketch);
        }
        {
            var Q0;
            Q0=makeQuery(id+"F18.imprint","IMPRINT",FACE,{"disambiguationData":[TD([[makeQuery(id+"F18.imprint","IMPRINT",EDGE,{"derivedFrom":sQuery(id+"F18.wireOp",EDGE,"E42.0")}),-1.0]])]});
            extrude(context, id + "F19", {"entities" : qUnion([Q0]), "operationType" : NewBodyOperationType.REMOVE, "oppositeDirection" : true, "depth" : 1.5 * mm});
        }
        {
            var Q0;
            Q0=makeQuery(id+"F15.opExtrude","CAP_FACE",FACE,{"disambiguationData":[OSD([sQuery(id+"F14.wireOp",EDGE,"E40")])],"isStart":true});
            var sketch = newSketch(context, id + "F20", { "sketchPlane" : qUnion([Q0])});
            skCircle(sketch, "E43.cCircle", {"center": v(-28.37, 0) * mm, "radius": 1.5 * mm, "construction": true});
            skLineSegment(sketch, "E43.0", {"start": v(-27.5, -1.5) * mm, "end": v(-29.24, -1.5) * mm});
            skLineSegment(sketch, "E43.1", {"start": v(-29.24, -1.5) * mm, "end": v(-30.1, 0) * mm});
            skLineSegment(sketch, "E43.2", {"start": v(-30.1, 0) * mm, "end": v(-29.24, 1.5) * mm});
            skLineSegment(sketch, "E43.3", {"start": v(-29.24, 1.5) * mm, "end": v(-27.5, 1.5) * mm});
            skLineSegment(sketch, "E43.4", {"start": v(-27.5, 1.5) * mm, "end": v(-26.63, 0) * mm});
            skLineSegment(sketch, "E43.5", {"start": v(-26.63, 0) * mm, "end": v(-27.5, -1.5) * mm});
            skPoint(sketch, "E43.0.midPoint", {"position": v(-28.37, -1.5) * mm});
            skSolve(sketch);
        }
        {
            var Q0;
            Q0=qSketchRegion(id+"F20",true);
            extrude(context, id + "F21", {"entities" : qUnion([Q0]), "operationType" : NewBodyOperationType.REMOVE, "oppositeDirection" : true, "depth" : 1.5 * mm});
        }
        {
            var Q0;
            Q0=makeQuery(id+"F15.opExtrude","SWEPT_BODY",BODY,{"disambiguationData":[OSD([sQuery(id+"F14.wireOp",EDGE,"E40")])]});
            transform(context, id + "F22", {"entities" : qUnion([Q0]), "transformType" : TransformType.TRANSLATION_3D, "dx" : 10 * mm, "dy" : 0 * mm, "dz" : 0 * mm, "makeCopy" : true});
        }
        {
            var Q0;
            Q0=makeQuery(id+"F22.opPattern","COPY",FACE,{"derivedFrom":makeQuery(id+"F17.opExtrude","CAP_FACE",FACE,{"disambiguationData":[OSD([sQuery(id+"F16.wireOp",EDGE,"E41")])],"isStart":false}),"instanceName":"1"});
            var sketch = newSketch(context, id + "F23", { "sketchPlane" : qUnion([Q0])});
            skCircle(sketch, "E44.0", {"center": v(38.37, 0) * mm, "radius": 1.5 * mm});
            skSolve(sketch);
        }
        {
            var Q0;
            Q0=qSketchRegion(id+"F23",true);
            extrude(context, id + "F24", {"entities" : qUnion([Q0]), "operationType" : NewBodyOperationType.REMOVE, "oppositeDirection" : true, "depth" : 8 * mm});
        }
        {
            var Q0;
            Q0=qCreatedBy(makeId("Top.planeOp"),FACE);
            var sketch = newSketch(context, id + "F25", { "sketchPlane" : qUnion([Q0])});
            skCircle(sketch, "E45.cCircle", {"center": v(-50, 0) * mm, "radius": 6.5 * mm, "construction": true});
            skLineSegment(sketch, "E45.0", {"start": v(-46.25, -6.5) * mm, "end": v(-53.75, -6.5) * mm});
            skLineSegment(sketch, "E45.1", {"start": v(-53.75, -6.5) * mm, "end": v(-57.5, 0) * mm});
            skLineSegment(sketch, "E45.2", {"start": v(-57.5, 0) * mm, "end": v(-53.75, 6.5) * mm});
            skLineSegment(sketch, "E45.3", {"start": v(-53.75, 6.5) * mm, "end": v(-46.25, 6.5) * mm});
            skLineSegment(sketch, "E45.4", {"start": v(-46.25, 6.5) * mm, "end": v(-42.5, 0) * mm});
            skLineSegment(sketch, "E45.5", {"start": v(-42.5, 0) * mm, "end": v(-46.25, -6.5) * mm});
            skPoint(sketch, "E45.0.midPoint", {"position": v(-50, -6.5) * mm});
            skSolve(sketch);
        }
        {
            var Q0;
            Q0=qSketchRegion(id+"F25",true);
            extrude(context, id + "F26", {"entities" : qUnion([Q0]), "depth" : 6.8 * mm});
        }
        {
            var Q0;
            Q0=makeQuery(id+"F26.opExtrude","CAP_FACE",FACE,{"disambiguationData":[OSD([sQuery(id+"F25.wireOp",EDGE,"E45.0"),sQuery(id+"F25.wireOp",EDGE,"E45.1"),sQuery(id+"F25.wireOp",EDGE,"E45.2"),sQuery(id+"F25.wireOp",EDGE,"E45.3"),sQuery(id+"F25.wireOp",EDGE,"E45.4"),sQuery(id+"F25.wireOp",EDGE,"E45.5")])],"isStart":false});
            var sketch = newSketch(context, id + "F27", { "sketchPlane" : qUnion([Q0])});
            skCircle(sketch, "E46", {"center": v(-50, 0) * mm, "radius": 4 * mm});
            skLineSegment(sketch, "E47", {"start": v(-50, 6.5) * mm, "end": v(-50, -6.5) * mm, "construction": true});
            skSolve(sketch);
        }
        {
            var Q0;
            Q0=qSketchRegion(id+"F27",true);
            var Q1;
            Q1=makeQuery(id+"F26.opExtrude","CAP_FACE",FACE,{"disambiguationData":[OSD([sQuery(id+"F25.wireOp",EDGE,"E45.0"),sQuery(id+"F25.wireOp",EDGE,"E45.1"),sQuery(id+"F25.wireOp",EDGE,"E45.2"),sQuery(id+"F25.wireOp",EDGE,"E45.3"),sQuery(id+"F25.wireOp",EDGE,"E45.4"),sQuery(id+"F25.wireOp",EDGE,"E45.5")])],"isStart":true});
            extrude(context, id + "F28", {"entities" : qUnion([Q0, Q1]), "operationType" : NewBodyOperationType.REMOVE, "oppositeDirection" : true, "depth" : 7 * mm});
        }
        {
            var Q0;
            Q0=makeQuery(id+"F26.opExtrude","CAP_EDGE",EDGE,{"disambiguationData":[OSD([sQuery(id+"F25.wireOp",EDGE,"E45.3")])],"isStart":false});
            var Q1;
            Q1=makeQuery(id+"F26.opExtrude","CAP_EDGE",EDGE,{"disambiguationData":[OSD([sQuery(id+"F25.wireOp",EDGE,"E45.2")])],"isStart":false});
            var Q2;
            Q2=makeQuery(id+"F26.opExtrude","CAP_EDGE",EDGE,{"disambiguationData":[OSD([sQuery(id+"F25.wireOp",EDGE,"E45.1")])],"isStart":false});
            var Q3;
            Q3=makeQuery(id+"F26.opExtrude","CAP_EDGE",EDGE,{"disambiguationData":[OSD([sQuery(id+"F25.wireOp",EDGE,"E45.0")])],"isStart":false});
            var Q4;
            Q4=makeQuery(id+"F26.opExtrude","CAP_EDGE",EDGE,{"disambiguationData":[OSD([sQuery(id+"F25.wireOp",EDGE,"E45.5")])],"isStart":false});
            var Q5;
            Q5=makeQuery(id+"F26.opExtrude","CAP_EDGE",EDGE,{"disambiguationData":[OSD([sQuery(id+"F25.wireOp",EDGE,"E45.4")])],"isStart":false});
            var Q6;
            Q6=makeQuery(id+"F26.opExtrude","CAP_EDGE",EDGE,{"disambiguationData":[OSD([sQuery(id+"F25.wireOp",EDGE,"E45.4")])],"isStart":true});
            var Q7;
            Q7=makeQuery(id+"F26.opExtrude","CAP_EDGE",EDGE,{"disambiguationData":[OSD([sQuery(id+"F25.wireOp",EDGE,"E45.3")])],"isStart":true});
            var Q8;
            Q8=makeQuery(id+"F26.opExtrude","CAP_EDGE",EDGE,{"disambiguationData":[OSD([sQuery(id+"F25.wireOp",EDGE,"E45.2")])],"isStart":true});
            var Q9;
            Q9=makeQuery(id+"F26.opExtrude","CAP_EDGE",EDGE,{"disambiguationData":[OSD([sQuery(id+"F25.wireOp",EDGE,"E45.5")])],"isStart":true});
            var Q10;
            Q10=makeQuery(id+"F26.opExtrude","CAP_EDGE",EDGE,{"disambiguationData":[OSD([sQuery(id+"F25.wireOp",EDGE,"E45.0")])],"isStart":true});
            var Q11;
            Q11=makeQuery(id+"F26.opExtrude","CAP_EDGE",EDGE,{"disambiguationData":[OSD([sQuery(id+"F25.wireOp",EDGE,"E45.1")])],"isStart":true});
            fillet(context, id + "F29", {"entities" : qUnion([Q0, Q1, Q2, Q3, Q4, Q5, Q6, Q7, Q8, Q9, Q10, Q11]), "radius" : 1 * mm, "tangentPropagation" : true, "allowEdgeOverflow" : false});
        }
        {
            var Q0;
            Q0=qCreatedBy(makeId("Top.planeOp"),FACE);
            var sketch = newSketch(context, id + "F30", { "sketchPlane" : qUnion([Q0])});
            skCircle(sketch, "E48", {"center": v(-75, 0) * mm, "radius": 5.75 * mm});
            skSolve(sketch);
        }
        {
            var Q0;
            Q0=qSketchRegion(id+"F30",true);
            extrude(context, id + "F31", {"entities" : qUnion([Q0]), "depth" : 1 * mm});
        }
        {
            var Q0;
            Q0=makeQuery(id+"F31.opExtrude","CAP_FACE",FACE,{"disambiguationData":[OSD([sQuery(id+"F30.wireOp",EDGE,"E48")])],"isStart":false});
            var sketch = newSketch(context, id + "F32", { "sketchPlane" : qUnion([Q0])});
            skCircle(sketch, "E49", {"center": v(-75, 0) * mm, "radius": 5 * mm});
            skSolve(sketch);
        }
        {
            var Q0;
            Q0=qSketchRegion(id+"F32",true);
            extrude(context, id + "F33", {"entities" : qUnion([Q0]), "operationType" : NewBodyOperationType.ADD, "depth" : 3 * mm});
        }
        {
            var Q0;
            Q0=makeQuery(id+"F33.opExtrude","CAP_FACE",FACE,{"disambiguationData":[OSD([sQuery(id+"F32.wireOp",EDGE,"E49")])],"isStart":false});
            var sketch = newSketch(context, id + "F34", { "sketchPlane" : qUnion([Q0])});
            skCircle(sketch, "E50", {"center": v(-75, 0) * mm, "radius": 1.5 * mm});
            skSolve(sketch);
        }
        {
            var Q0;
            Q0=qSketchRegion(id+"F34",true);
            extrude(context, id + "F35", {"entities" : qUnion([Q0]), "operationType" : NewBodyOperationType.REMOVE, "oppositeDirection" : true, "depth" : 4 * mm});
        }
        {
            var Q0;
            Q0=qCreatedBy(makeId("Top.planeOp"),FACE);
            var sketch = newSketch(context, id + "F36", { "sketchPlane" : qUnion([Q0])});
            skCircle(sketch, "E51", {"center": v(60, 0) * mm, "radius": 8 * mm});
            skSolve(sketch);
        }
        {
            var Q0;
            Q0=qSketchRegion(id+"F36",true);
            extrude(context, id + "F37", {"entities" : qUnion([Q0]), "depth" : 5 * mm});
        }
        {
            var Q0;
            Q0=makeQuery(id+"F37.opExtrude","CAP_FACE",FACE,{"disambiguationData":[OSD([sQuery(id+"F36.wireOp",EDGE,"E51")])],"isStart":false});
            var sketch = newSketch(context, id + "F38", { "sketchPlane" : qUnion([Q0])});
            skCircle(sketch, "E52", {"center": v(60, 0) * mm, "radius": 2.5 * mm});
            skSolve(sketch);
        }
        {
            var Q0;
            Q0=qSketchRegion(id+"F38",true);
            extrude(context, id + "F39", {"entities" : qUnion([Q0]), "operationType" : NewBodyOperationType.REMOVE, "oppositeDirection" : true, "depth" : 5 * mm});
        }
        {
            var Q0;
            Q0=qCreatedBy(makeId("Top.planeOp"),FACE);
            var sketch = newSketch(context, id + "F40", { "sketchPlane" : qUnion([Q0])});
            skCircle(sketch, "E53", {"center": v(85, 0) * mm, "radius": 4 * mm});
            skSolve(sketch);
        }
        {
            var Q0;
            Q0=qSketchRegion(id+"F40",true);
            extrude(context, id + "F41", {"entities" : qUnion([Q0]), "depth" : 185 * mm});
        }
    });
